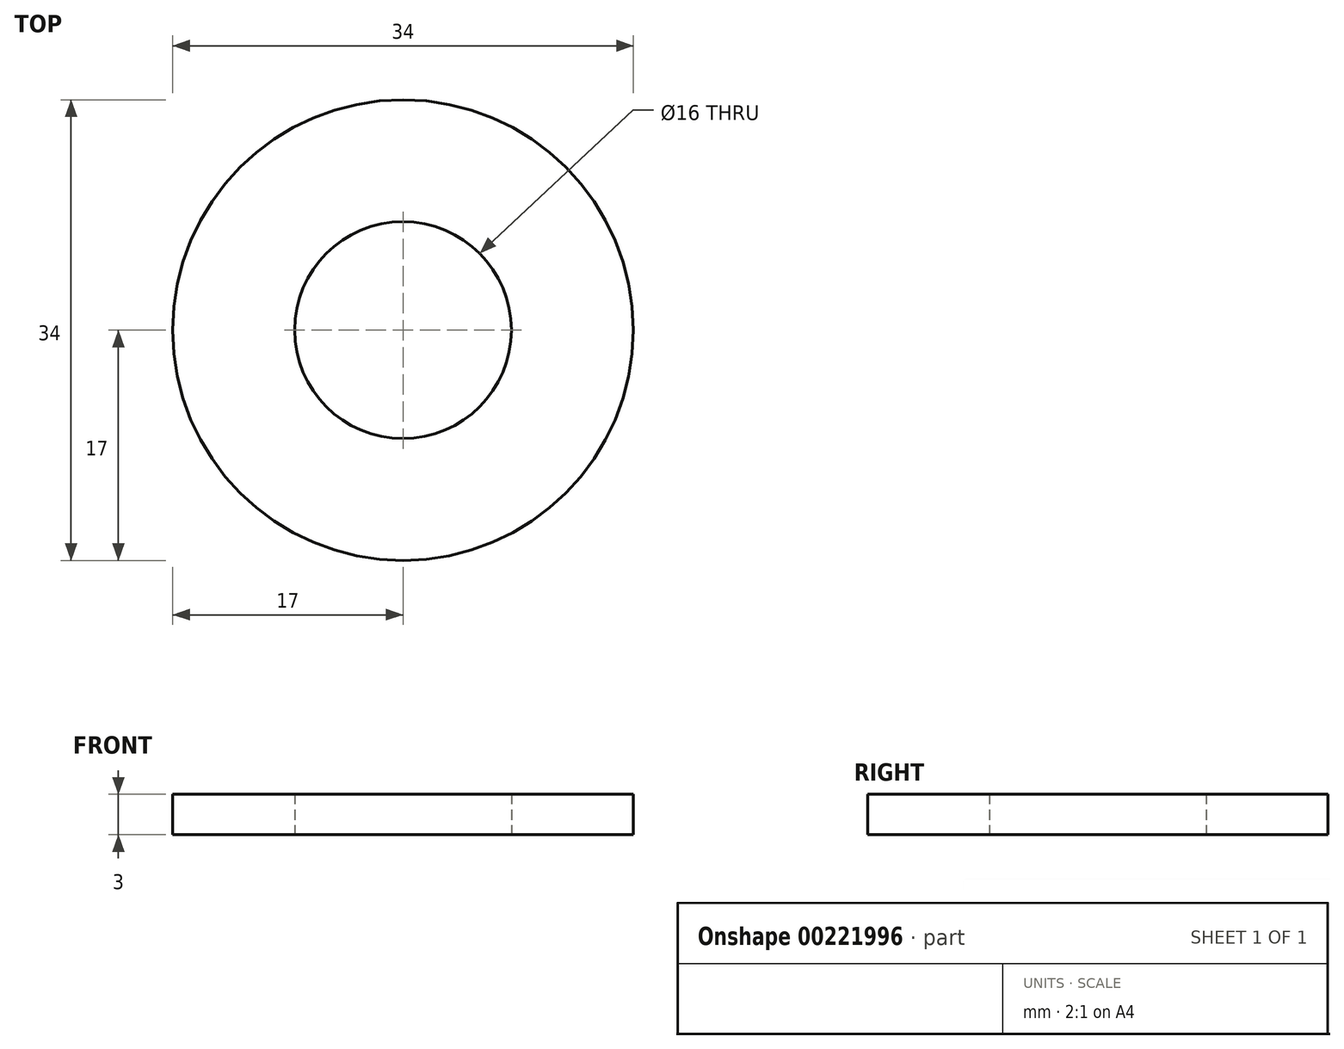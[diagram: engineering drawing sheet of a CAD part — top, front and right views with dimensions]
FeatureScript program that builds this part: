
annotation { "Feature Type Name" : "Feature", "Feature Type Description" : "" }
export const myFeature = defineFeature(function(context is Context, id is Id, definition is map)
    precondition{}
    {
        {
            var Q0;
            Q0=qCreatedBy(makeId("Top.planeOp"),FACE);
            var sketch = newSketch(context, id + "F0", { "sketchPlane" : qUnion([Q0])});
            skCircle(sketch, "E0", {"center": v(0, 0) * mm, "radius": 8 * mm});
            skCircle(sketch, "E1", {"center": v(0, 0) * mm, "radius": 17 * mm});
            skSolve(sketch);
        }
        {
            var Q0;
            Q0 = qSketchRegion(id + "F0", true);
            extrude(context, id + "F1", {"entities" : qUnion([Q0]), "depth" : 3 * mm});
        }
    });
